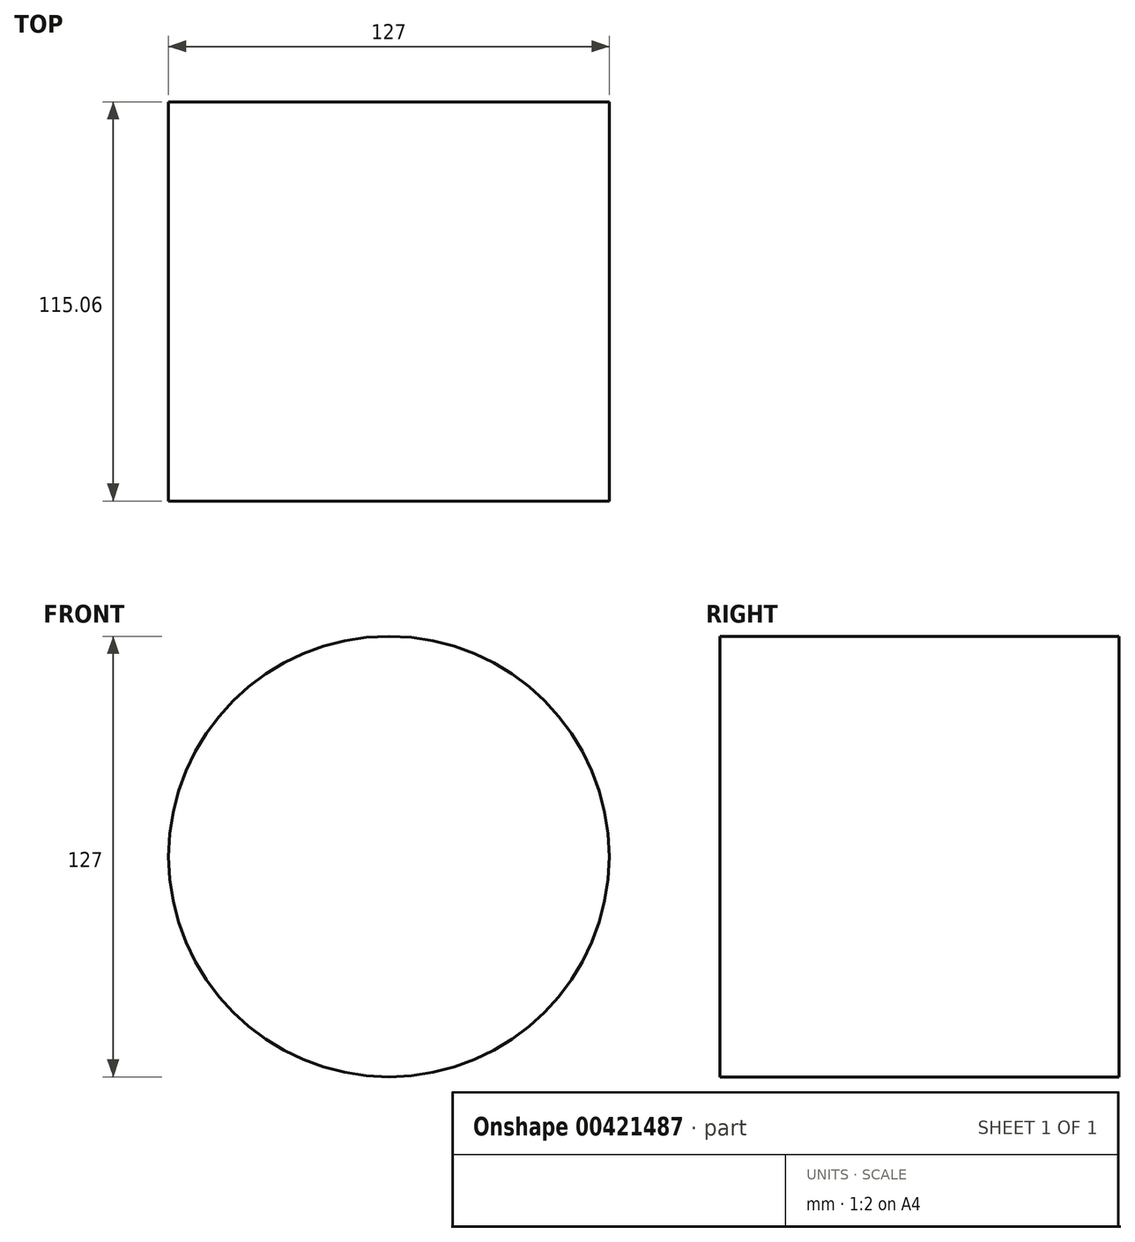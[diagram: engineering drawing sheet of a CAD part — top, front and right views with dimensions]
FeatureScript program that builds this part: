
annotation { "Feature Type Name" : "Feature", "Feature Type Description" : "" }
export const myFeature = defineFeature(function(context is Context, id is Id, definition is map)
    precondition{}
    {
        {
            var Q0;
            Q0=qCreatedBy(makeId("Front.planeOp"),FACE);
            var sketch = newSketch(context, id + "F0", { "sketchPlane" : qUnion([Q0])});
            skCircle(sketch, "E0", {"center": v(0, 0) * mm, "radius": 63.5 * mm});
            skSolve(sketch);
        }
        {
            var Q0;
            Q0 = qSketchRegion(id + "F0", true);
            extrude(context, id + "F1", {"entities" : qUnion([Q0]), "depth" : 115.06 * mm});
        }
    });
